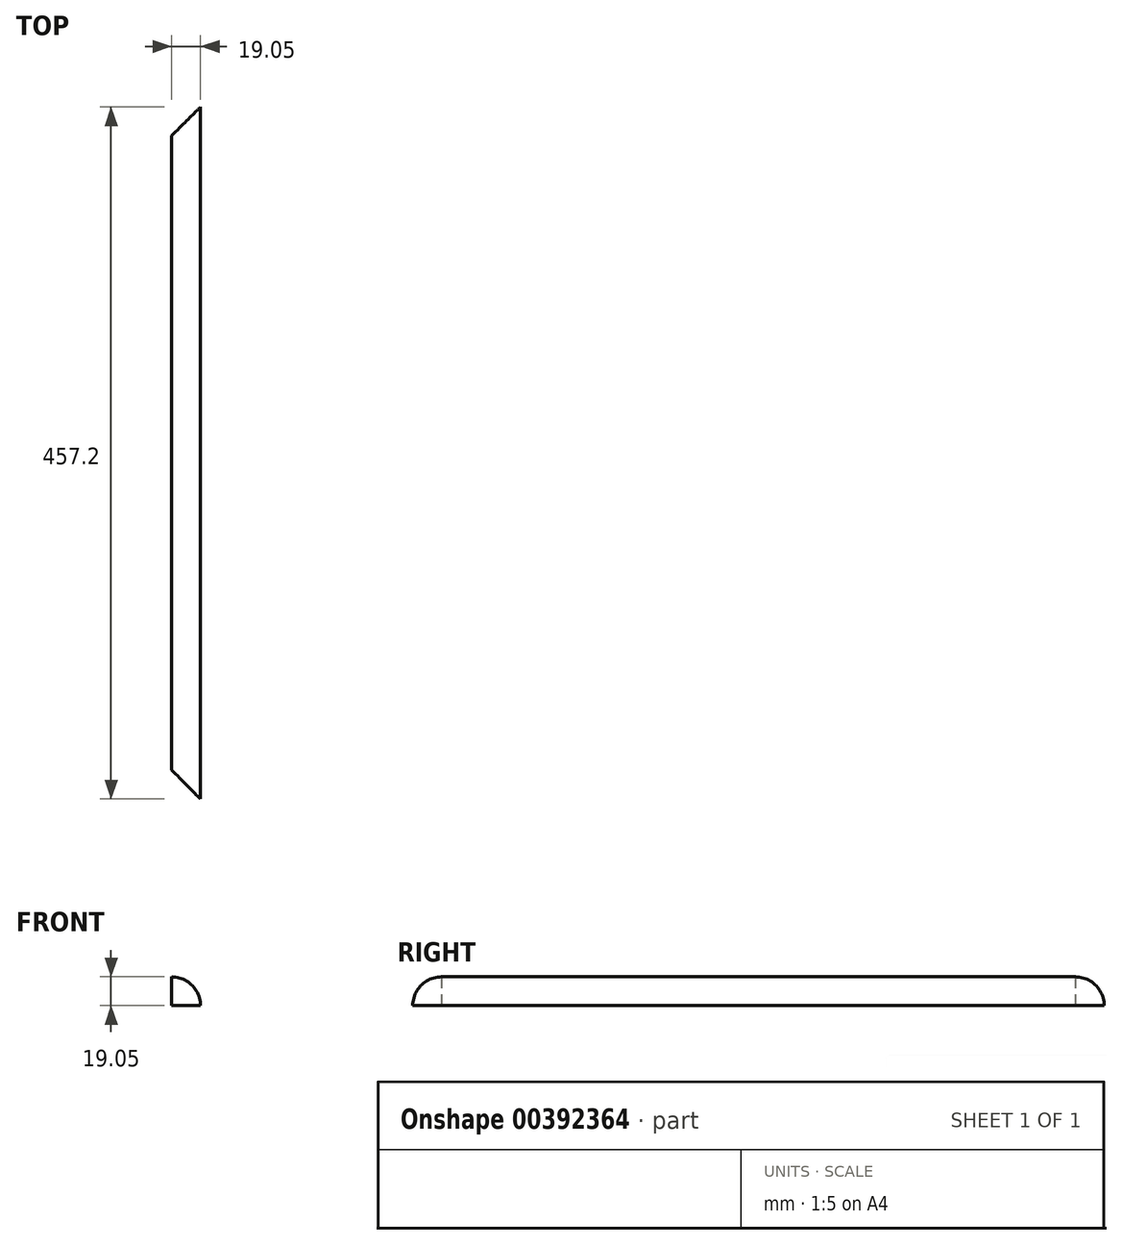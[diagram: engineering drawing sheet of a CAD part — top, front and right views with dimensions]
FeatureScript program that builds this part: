
annotation { "Feature Type Name" : "Feature", "Feature Type Description" : "" }
export const myFeature = defineFeature(function(context is Context, id is Id, definition is map)
    precondition{}
    {
        {
            var Q0;
            Q0=qCreatedBy(makeId("Front.planeOp"),FACE);
            var sketch = newSketch(context, id + "F0", { "sketchPlane" : qUnion([Q0])});
            skLineSegment(sketch, "E0.bottom", {"start": v(0, 0) * mm, "end": v(19.05, 0) * mm});
            skLineSegment(sketch, "E0.left", {"start": v(0, 0) * mm, "end": v(0, 19.05) * mm});
            skArc(sketch, "E1", {"start": v(19.05, 0) * mm, "mid": v(13.47, 13.47) * mm, "end": v(0, 19.05) * mm});
            skSolve(sketch);
        }
        {
            var Q0;
            Q0=makeQuery(id+"F0.imprint","IMPRINT",FACE,{"disambiguationData":[TD([[makeQuery(id+"F0.imprint","IMPRINT",EDGE,{"derivedFrom":sQuery(id+"F0.wireOp",EDGE,"E0.bottom")}),1.0]])]});
            extrude(context, id + "F1", {"entities" : qUnion([Q0]), "depth" : 457.2 * mm});
        }
        {
            var Q0;
            Q0=makeQuery(id+"F1.opExtrude","SWEPT_FACE",FACE,{"disambiguationData":[OSD([sQuery(id+"F0.wireOp",EDGE,"E0.bottom")])]});
            var sketch = newSketch(context, id + "F2", { "sketchPlane" : qUnion([Q0])});
            skLineSegment(sketch, "E2", {"start": v(19.05, 0) * mm, "end": v(0, 19.05) * mm});
            skLineSegment(sketch, "E3", {"start": v(19.05, 457.2) * mm, "end": v(0, 438.15) * mm});
            skSolve(sketch);
        }
        {
            var Q0;
            {var subQ0=sQuery(id+"F2.wireOp",EDGE,"E2");Q0=makeQuery(id+"F2.imprint","IMPRINT",FACE,{"disambiguationData":[TD([[makeQuery(id+"F2.imprint","IMPRINT",EDGE,{"derivedFrom":subQ0}),1.0]])]});}
            var Q1;
            {var subQ0=sQuery(id+"F2.wireOp",EDGE,"E3");Q1=makeQuery(id+"F2.imprint","IMPRINT",FACE,{"disambiguationData":[TD([[makeQuery(id+"F2.imprint","IMPRINT",EDGE,{"derivedFrom":subQ0}),-1.0]])]});}
            extrude(context, id + "F3", {"entities" : qUnion([Q0, Q1]), "operationType" : NewBodyOperationType.REMOVE, "oppositeDirection" : true, "depth" : 25.4 * mm});
        }
    });
